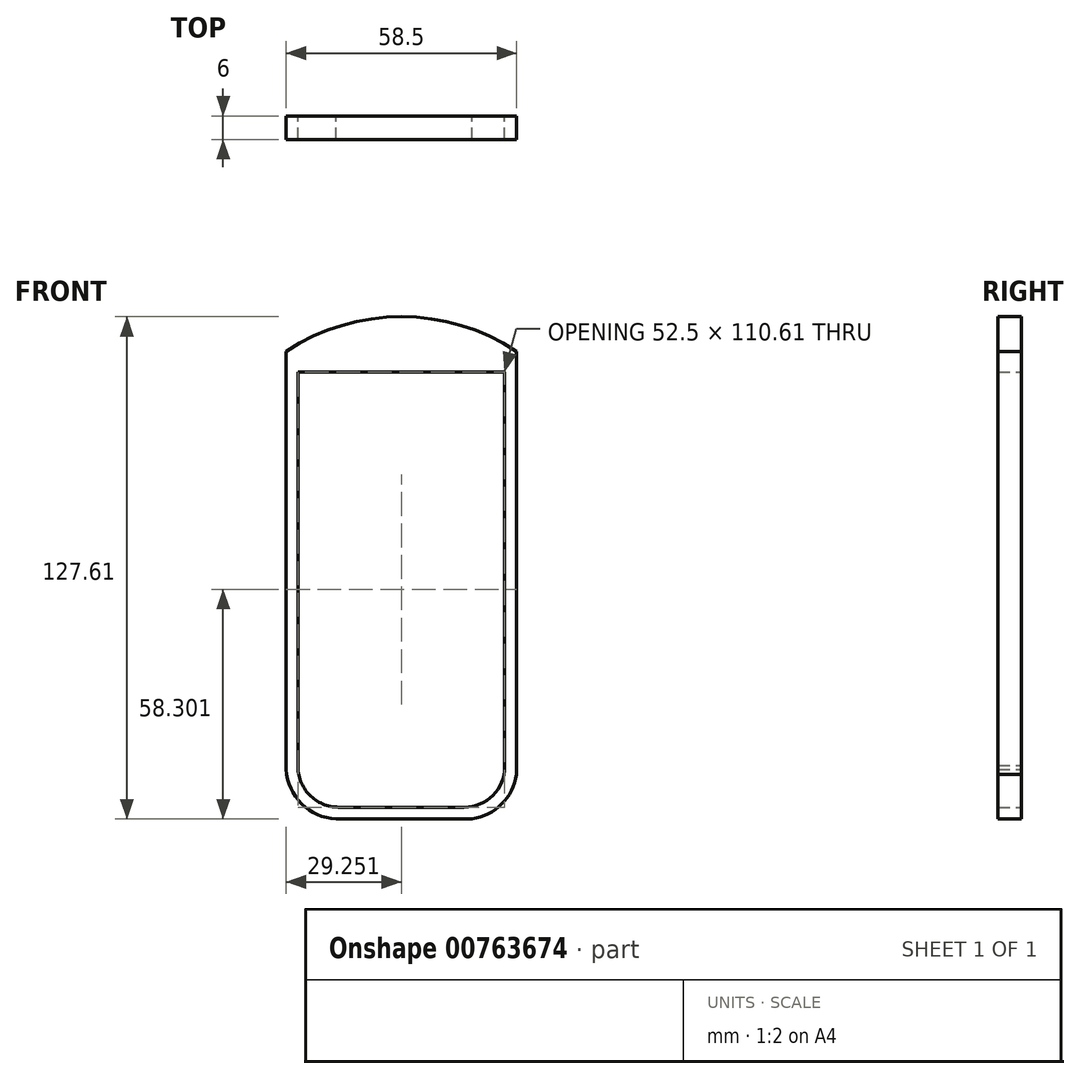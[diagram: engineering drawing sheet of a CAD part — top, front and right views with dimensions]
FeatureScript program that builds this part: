
annotation { "Feature Type Name" : "Feature", "Feature Type Description" : "" }
export const myFeature = defineFeature(function(context is Context, id is Id, definition is map)
    precondition{}
    {
        {
            var Q0;
            Q0=qCreatedBy(makeId("Front.planeOp"),FACE);
            var sketch = newSketch(context, id + "F0", { "sketchPlane" : qUnion([Q0])});
            skLineSegment(sketch, "E0", {"start": v(-35.89, -59.3) * mm, "end": v(-3.92, -59.3) * mm});
            skLineSegment(sketch, "E1", {"start": v(6.35, -49.03) * mm, "end": v(6.35, 51.3) * mm});
            skPoint(sketch, "E2.visualSharp", {"position": v(-43.07, -59.3) * mm});
            skArc(sketch, "E2.filletArc", {"start": v(-46.15, -48.72) * mm, "mid": v(-43.26, -56.18) * mm, "end": v(-35.89, -59.3) * mm});
            skPoint(sketch, "E3.visualSharp", {"position": v(6.35, -59.3) * mm});
            skArc(sketch, "E3.filletArc", {"start": v(-3.92, -59.3) * mm, "mid": v(3.34, -56.3) * mm, "end": v(6.35, -49.03) * mm});
            skArc(sketch, "E4", {"start": v(9.35, 56.5) * mm, "mid": v(-19.9, 65.3) * mm, "end": v(-49.15, 56.5) * mm});
            skLineSegment(sketch, "E5", {"start": v(-46.15, -48.72) * mm, "end": v(-46.15, 51.3) * mm});
            skArc(sketch, "E6.2", {"start": v(-1.95, -62.3) * mm, "mid": v(5.57, -58.52) * mm, "end": v(9.35, -51) * mm});
            skLineSegment(sketch, "E6.3", {"start": v(-36.45, -62.3) * mm, "end": v(-1.95, -62.3) * mm});
            skArc(sketch, "E6.4", {"start": v(-49.15, -49.7) * mm, "mid": v(-45.24, -58.46) * mm, "end": v(-36.45, -62.3) * mm});
            skLineSegment(sketch, "E7", {"start": v(-46.15, 51.3) * mm, "end": v(6.35, 51.3) * mm});
            skLineSegment(sketch, "E8", {"start": v(-49.15, -49.7) * mm, "end": v(-49.15, 56.5) * mm});
            skLineSegment(sketch, "E9", {"start": v(9.35, -51) * mm, "end": v(9.35, 56.5) * mm});
            skSolve(sketch);
        }
        {
            var Q0;
            Q0 = qSketchRegion(id + "F0", true);
            extrude(context, id + "F1", {"entities" : qUnion([Q0]), "depth" : 6 * mm, "offsetDistance" : 25 * mm});
        }
    });
